FCSTD DOCUMENT  (FreeCAD 0.19R)
Label: plate_stand
License: All rights reserved
LicenseURL: http://en.wikipedia.org/wiki/All_rights_reserved
objects: App::Link×15, App::DocumentObjectGroup×2, PartDesign::CoordinateSystem×1, App::FeaturePython×1, App::Part×1
note: 1 computed .brp shape members not serialized (recipe doc carries the construction recipe); baked Part::Feature solids carry a one-line shape summary decoded from their .brp
EXTERNAL_REF file=column_60_60.FCStd obj=LCS_0
EXTERNAL_REF file=column_60_60.FCStd obj=____________Body
EXTERNAL_REF file=bridge_front.FCStd obj=LCS_middle
EXTERNAL_REF file=column_60_60.FCStd obj=LCS_bottom
EXTERNAL_REF file=bridge_front.FCStd obj=Body
EXTERNAL_REF file=bridge_front.FCStd obj=LCS_0
EXTERNAL_REF file=column_50_25.FCStd obj=LCS_bottom
EXTERNAL_REF file=column_50_25.FCStd obj=SmallColumnBody
EXTERNAL_REF file=column_60_60.FCStd obj=LCS_bottom_right
EXTERNAL_REF file=bridge_front.FCStd obj=LCS_0001
EXTERNAL_REF file=column_50_25.FCStd obj=LCS_bottom_narrow_2
EXTERNAL_REF file=bridge_front.FCStd obj=Body_bridge_side
EXTERNAL_REF file=column_50_25.FCStd obj=LCS_bottom_narrow1
EXTERNAL_REF file=bridge_front.FCStd obj=LCS_opp_side
EXTERNAL_REF file=bridge_front.FCStd obj=LCS_1
EXTERNAL_REF file=column_60_60.FCStd obj=LCS_1
EXTERNAL_REF file=bridge_front.FCStd obj=Body_2
EXTERNAL_REF file=column_60_60.FCStd obj=LCS_3
EXTERNAL_REF file=column_60_60.FCStd obj=LCS_2
EXTERNAL_REF file=column_60_60.FCStd obj=LCS_4

FEATURE [App::DocumentObjectGroup] Parts
FEATURE [PartDesign::CoordinateSystem] LCS_Origin
  AttacherType = Attacher::AttachEngine3D
  MapMode = 2
  Support = -> [X_Axis]
FEATURE [App::DocumentObjectGroup] Constraints
FEATURE [App::FeaturePython] Variables  # WARN: FeaturePython — macro-defined, semantics opaque (R4)
FEATURE [App::Link] column_60_60_ColumnBody
  AssemblyType = Asm4EE
  AttachedBy = #LCS_0
  AttachedTo = Parent Assembly#LCS_Origin
  LinkedObject = -> <external column_60_60.FCStd>#____________Body
  expr: Placement = LCS_Origin.Placement * AttachmentOffset * column_60_60#LCS_0.Placement ^ -1
FEATURE [App::Link] Unnamed_FrontBridgeBody
  AssemblyType = Asm4EE
  AttachedBy = #LCS_middle
  AttachedTo = column_60_60_ColumnBody#LCS_bottom
  AttachmentOffset = pos=(0,0,0) rot=(0,1,0;3.14159rad)
  LinkPlacement = pos=(-1.18e-14,-97.5,25) rot=(0,0,1;1.5708rad)
  LinkedObject = -> <external bridge_front.FCStd>#Body
  Placement = pos=(-1.18e-14,-97.5,25) rot=(0,0,1;1.5708rad)
  expr: Placement = column_60_60_ColumnBody.Placement * column_60_60#LCS_bottom.Placement * AttachmentOffset * bridge_front#LCS_middle.Placement ^ -1
FEATURE [App::Link] column_50_25_SmallColumnBody
  AssemblyType = Asm4EE
  AttachedBy = #LCS_bottom
  AttachedTo = Unnamed_FrontBridgeBody#LCS_0
  AttachmentOffset = pos=(0,0,0) rot=(-0.57735,-0.57735,-0.57735;4.18879rad)
  LinkPlacement = pos=(6.8e-15,-110,2.49e-14) rot=(0,0,-1;3.14159rad)
  LinkedObject = -> <external column_50_25.FCStd>#SmallColumnBody
  Placement = pos=(6.8e-15,-110,2.49e-14) rot=(0,0,-1;3.14159rad)
  expr: Placement = Unnamed_FrontBridgeBody.Placement * bridge_front#LCS_0.Placement * AttachmentOffset * column_50_25#LCS_bottom.Placement ^ -1
FEATURE [App::Link] bridge_front_FrontBridgeBody
  AssemblyType = Asm4EE
  AttachedBy = #LCS_middle
  AttachedTo = column_60_60_ColumnBody#LCS_bottom_right
  AttachmentOffset = pos=(0,0,0) rot=(1,0,0;3.14159rad)
  LinkPlacement = pos=(1.106e-12,97.5,25) rot=(-0.707107,0.707107,0;3.14159rad)
  LinkedObject = -> <external bridge_front.FCStd>#Body
  Placement = pos=(1.106e-12,97.5,25) rot=(-0.707107,0.707107,0;3.14159rad)
  expr: Placement = column_60_60_ColumnBody.Placement * column_60_60#LCS_bottom_right.Placement * AttachmentOffset * bridge_front#LCS_middle.Placement ^ -1
FEATURE [App::Link] column_50_25_SmallColumnBody001
  AssemblyType = Asm4EE
  AttachedBy = #LCS_bottom
  AttachedTo = bridge_front_FrontBridgeBody#LCS_0
  AttachmentOffset = pos=(0,0,0) rot=(0.57735,-0.57735,0.57735;4.18879rad)
  LinkPlacement = pos=(1.2532e-12,110,-2.84e-14) rot=(0,0,1;0rad)
  LinkedObject = -> <external column_50_25.FCStd>#SmallColumnBody
  Placement = pos=(1.2532e-12,110,-2.84e-14) rot=(0,0,1;0rad)
  expr: Placement = bridge_front_FrontBridgeBody.Placement * bridge_front#LCS_0.Placement * AttachmentOffset * column_50_25#LCS_bottom.Placement ^ -1
FEATURE [App::Link] bridge_front_Body_bridge_side
  AssemblyType = Asm4EE
  AttachedBy = #LCS_0001
  AttachedTo = column_50_25_SmallColumnBody#LCS_bottom_narrow_2
  AttachmentOffset = pos=(0,0,0) rot=(1,0,0;4.71239rad)
  LinkPlacement = pos=(25,-110,25) rot=(0,0,1;1.5708rad)
  LinkedObject = -> <external bridge_front.FCStd>#Body_bridge_side
  Placement = pos=(25,-110,25) rot=(0,0,1;1.5708rad)
  expr: Placement = column_50_25_SmallColumnBody.Placement * column_50_25#LCS_bottom_narrow_2.Placement * AttachmentOffset * bridge_front#LCS_0001.Placement ^ -1
FEATURE [App::Link] bridge_front_Body_bridge_side001
  AssemblyType = Asm4EE
  AttachedBy = #LCS_0001
  AttachedTo = column_50_25_SmallColumnBody001#LCS_bottom_narrow1
  AttachmentOffset = pos=(0,0,0) rot=(1,0,0;4.71239rad)
  LinkPlacement = pos=(25,110,25) rot=(0,0,-1;4.71239rad)
  LinkedObject = -> <external bridge_front.FCStd>#Body_bridge_side
  Placement = pos=(25,110,25) rot=(0,0,-1;4.71239rad)
  expr: Placement = column_50_25_SmallColumnBody001.Placement * column_50_25#LCS_bottom_narrow1.Placement * AttachmentOffset * bridge_front#LCS_0001.Placement ^ -1
FEATURE [App::Link] column_60_60_ColumnBody001
  AssemblyType = Asm4EE
  AttachedBy = #LCS_bottom_right
  AttachedTo = bridge_front_Body_bridge_side#LCS_opp_side
  AttachmentOffset = pos=(0,0,0) rot=(0,1,0;3.14159rad)
  LinkPlacement = pos=(220,-110,2.771e-13) rot=(0,0,1;1.5708rad)
  LinkedObject = -> <external column_60_60.FCStd>#____________Body
  Placement = pos=(220,-110,2.771e-13) rot=(0,0,1;1.5708rad)
  expr: Placement = bridge_front_Body_bridge_side.Placement * bridge_front#LCS_opp_side.Placement * AttachmentOffset * column_60_60#LCS_bottom_right.Placement ^ -1
FEATURE [App::Link] column_60_60_ColumnBody002
  AssemblyType = Asm4EE
  AttachedBy = #LCS_bottom
  AttachedTo = bridge_front_Body_bridge_side001#LCS_opp_side
  AttachmentOffset = pos=(0,0,0) rot=(0,1,0;3.14159rad)
  LinkPlacement = pos=(220,110,1.315e-13) rot=(0,0,-1;1.5708rad)
  LinkedObject = -> <external column_60_60.FCStd>#____________Body
  Placement = pos=(220,110,1.315e-13) rot=(0,0,-1;1.5708rad)
  expr: Placement = bridge_front_Body_bridge_side001.Placement * bridge_front#LCS_opp_side.Placement * AttachmentOffset * column_60_60#LCS_bottom.Placement ^ -1
FEATURE [App::Link] bridge_front_Body_bridge_back
  AssemblyType = Asm4EE
  AttachedBy = #LCS_1
  AttachedTo = column_60_60_ColumnBody002#LCS_1
  AttachmentOffset = pos=(0,0,0) rot=(0,1,0;3.14159rad)
  LinkPlacement = pos=(220,-80,25) rot=(0,0,1;3.14159rad)
  LinkedObject = -> <external bridge_front.FCStd>#Body_2
  Placement = pos=(220,-80,25) rot=(0,0,1;3.14159rad)
  expr: Placement = column_60_60_ColumnBody002.Placement * column_60_60#LCS_1.Placement * AttachmentOffset * bridge_front#LCS_1.Placement ^ -1
FEATURE [App::Link] bridge_front_Body_bridge_back001
  AssemblyType = Asm4EE
  AttachedBy = #LCS_1
  AttachedTo = column_60_60_ColumnBody001#LCS_3
  AttachmentOffset = pos=(0,0,0) rot=(0.707107,0,0.707107;3.14159rad)
  LinkPlacement = pos=(223,80,675) rot=(0,1,0;3.14159rad)
  LinkedObject = -> <external bridge_front.FCStd>#Body_2
  Placement = pos=(223,80,675) rot=(0,1,0;3.14159rad)
  expr: Placement = column_60_60_ColumnBody001.Placement * column_60_60#LCS_3.Placement * AttachmentOffset * bridge_front#LCS_1.Placement ^ -1
FEATURE [App::Link] bridge_front_Body_bridge_side002
  AssemblyType = Asm4EE
  AttachedBy = #LCS_0001
  AttachedTo = column_60_60_ColumnBody001#LCS_2
  AttachmentOffset = pos=(0,0,0) rot=(-0.57735,-0.57735,0.57735;4.18879rad)
  LinkPlacement = pos=(190,-107,675) rot=(0.707107,0.707107,0;3.14159rad)
  LinkedObject = -> <external bridge_front.FCStd>#Body_bridge_side
  Placement = pos=(190,-107,675) rot=(0.707107,0.707107,0;3.14159rad)
  expr: Placement = column_60_60_ColumnBody001.Placement * column_60_60#LCS_2.Placement * AttachmentOffset * bridge_front#LCS_0001.Placement ^ -1
FEATURE [App::Link] bridge_front_Body_bridge_side003
  AssemblyType = Asm4EE
  AttachedBy = #LCS_0001
  AttachedTo = column_60_60_ColumnBody002#LCS_4
  AttachmentOffset = pos=(0,0,0) rot=(0.57735,0.57735,0.57735;4.18879rad)
  LinkPlacement = pos=(190,113,675) rot=(0,0,1;4.71239rad)
  LinkedObject = -> <external bridge_front.FCStd>#Body_bridge_side
  Placement = pos=(190,113,675) rot=(0,0,1;4.71239rad)
  expr: Placement = column_60_60_ColumnBody002.Placement * column_60_60#LCS_4.Placement * AttachmentOffset * bridge_front#LCS_0001.Placement ^ -1
FEATURE [App::Link] bridge_front_FrontBridgeBody001
  AssemblyType = Asm4EE
  AttachedBy = #LCS_middle
  AttachedTo = column_60_60_ColumnBody#LCS_2
  AttachmentOffset = pos=(0,0,0) rot=(0,1,0;1.5708rad)
  LinkPlacement = pos=(3,97.5,675) rot=(0,0,1;4.71239rad)
  LinkedObject = -> <external bridge_front.FCStd>#Body
  Placement = pos=(3,97.5,675) rot=(0,0,1;4.71239rad)
  expr: Placement = column_60_60_ColumnBody.Placement * column_60_60#LCS_2.Placement * AttachmentOffset * bridge_front#LCS_middle.Placement ^ -1
FEATURE [App::Link] bridge_front_FrontBridgeBody002
  AssemblyType = Asm4EE
  AttachedBy = #LCS_middle
  AttachedTo = column_60_60_ColumnBody#LCS_4
  AttachmentOffset = pos=(0,0,0) rot=(0,1,0;1.5708rad)
  LinkPlacement = pos=(-3,-97.5,675) rot=(0,0,1;1.5708rad)
  LinkedObject = -> <external bridge_front.FCStd>#Body
  Placement = pos=(-3,-97.5,675) rot=(0,0,1;1.5708rad)
  expr: Placement = column_60_60_ColumnBody.Placement * column_60_60#LCS_4.Placement * AttachmentOffset * bridge_front#LCS_middle.Placement ^ -1
FEATURE [App::Part] Model
  Configuration = 0
  Group = -> [LCS_Origin,Constraints,Variables,column_60_60_ColumnBody,Unnamed_FrontBridgeBody,column_50_25_SmallColumnBody,bridge_front_FrontBridgeBody,column_50_25_SmallColumnBody001,bridge_front_Body_bridge_side,bridge_front_Body_bridge_side001,column_60_60_ColumnBody001,column_60_60_ColumnBody002,bridge_front_Body_bridge_back,bridge_front_Body_bridge_back001,bridge_front_Body_bridge_side002,+3 more]
  Origin = -> Origin
  Type = Assembly4 Model

RESOLVED EXTERNAL PARTS (link-assembly join: the EXTERNAL_REF files above that resolve inside this repo's crawl, each included once):
---- part bridge_front.FCStd = doc fcstd_2d3e780000c6 ----
FCSTD DOCUMENT  (FreeCAD 0.19R)
Label: bridge_front
License: All rights reserved
LicenseURL: http://en.wikipedia.org/wiki/All_rights_reserved
objects: PartDesign::CoordinateSystem×6, Sketcher::SketchObject×3, PartDesign::Pad×3, PartDesign::Body×3
note: 18 computed .brp shape members not serialized (recipe doc carries the construction recipe); baked Part::Feature solids carry a one-line shape summary decoded from their .brp

FEATURE [PartDesign::CoordinateSystem] LCS_0
  AttacherType = Attacher::AttachEngine3D
  MapMode = 2
  Support = -> [X_Axis]
FEATURE [Sketcher::SketchObject] Sketch
  FullyConstrained = true
  MapMode = 5
  Placement = pos=(0,0,0) rot=(0.57735,0.57735,0.57735;2.0944rad)
  Support = -> [YZ_Plane]
  sketch-geometry (8):
    g0: LineSegment StartX=-8 StartY=20 StartZ=0 EndX=8 EndY=20 EndZ=0
    g1: LineSegment StartX=10 StartY=18 StartZ=0 EndX=10 EndY=-18 EndZ=0
    g2: LineSegment StartX=8 StartY=-20 StartZ=0 EndX=-8 EndY=-20 EndZ=0
    g3: LineSegment StartX=-10 StartY=-18 StartZ=0 EndX=-10 EndY=18 EndZ=0
    g4: ArcOfCircle CenterX=-8 CenterY=18 CenterZ=0 NormalX=0 NormalY=0 NormalZ=1 AngleXU=0 Radius=2 StartAngle=1.5708 EndAngle=3.14159
    g5: ArcOfCircle CenterX=-8 CenterY=-18 CenterZ=0 NormalX=0 NormalY=0 NormalZ=1 AngleXU=0 Radius=2 StartAngle=3.14159 EndAngle=4.71239
    g6: ArcOfCircle CenterX=8 CenterY=-18 CenterZ=0 NormalX=0 NormalY=0 NormalZ=1 AngleXU=0 Radius=2 StartAngle=4.71239 EndAngle=6.28319
    g7: ArcOfCircle CenterX=8 CenterY=18 CenterZ=0 NormalX=0 NormalY=0 NormalZ=1 AngleXU=0 Radius=2 StartAngle=-4.71e-14 EndAngle=1.5708
  constraints (18):
    c: Horizontal(g0)
    c: Horizontal(g2)
    c: Vertical(g1)
    c: Vertical(g3)
    c: Tangent(g0,g4) = 1.5708
    c: Tangent(g3,g4) = 1.5708
    c: Tangent(g3,g5) = 1.5708
    c: Tangent(g2,g5) = 1.5708
    c: Tangent(g1,g6) = 1.5708
    c: Tangent(g2,g6) = 1.5708
    c: Tangent(g0,g7) = 1.5708
    c: Tangent(g1,g7) = 1.5708
    c: Radius(g6) = 2
    c: Equal(g6,g5)
    c: DistanceY(g2,g0) = 40
    c: DistanceX(g3,g1) = 20
    c: Symmetric(g3,g1,g-2)
    c: Symmetric(g2,g0,g-1)
FEATURE [PartDesign::Pad] Pad
  Direction = (1,1,1)
  Length = 67.5
  Length2 = 100
  Placement = pos=(0,0,0) rot=(0.57735,0.57735,0.57735;2.0944rad)
  Profile = -> Sketch
  Type = 0
FEATURE [PartDesign::CoordinateSystem] LCS_middle
  AttacherType = Attacher::AttachEngine3D
  MapMode = 5
  Placement = pos=(67.5,-3e-14,2.25e-14) rot=(0.57735,0.57735,0.57735;2.0944rad)
  Support = -> [Pad]
FEATURE [PartDesign::Body] Body  label="FrontBridgeBody"
  Group = -> [LCS_0,Sketch,Pad,LCS_middle]
  Origin = -> Origin
  Tip = -> Pad
FEATURE [PartDesign::CoordinateSystem] LCS_0001
  AttacherType = Attacher::AttachEngine3D
  MapMode = 2
  Support = -> [X_Axis001]
FEATURE [Sketcher::SketchObject] Sketch001
  FullyConstrained = true
  MapMode = 5
  Placement = pos=(0,0,0) rot=(1,0,0;1.5708rad)
  Support = -> [XZ_Plane001]
  sketch-geometry (8):
    g0: LineSegment StartX=-8 StartY=20 StartZ=0 EndX=8 EndY=20 EndZ=0
    g1: LineSegment StartX=10 StartY=18 StartZ=0 EndX=10 EndY=-18 EndZ=0
    g2: LineSegment StartX=8 StartY=-20 StartZ=0 EndX=-8 EndY=-20 EndZ=0
    g3: LineSegment StartX=-10 StartY=-18 StartZ=0 EndX=-10 EndY=18 EndZ=0
    g4: ArcOfCircle CenterX=-8 CenterY=-18 CenterZ=0 NormalX=0 NormalY=0 NormalZ=1 AngleXU=0 Radius=2 StartAngle=3.14159 EndAngle=4.71239
    g5: ArcOfCircle CenterX=8 CenterY=-18 CenterZ=0 NormalX=0 NormalY=0 NormalZ=1 AngleXU=0 Radius=2 StartAngle=4.71239 EndAngle=6.28319
    g6: ArcOfCircle CenterX=8 CenterY=18 CenterZ=0 NormalX=0 NormalY=0 NormalZ=1 AngleXU=0 Radius=2 StartAngle=0 EndAngle=1.5708
    g7: ArcOfCircle CenterX=-8 CenterY=18 CenterZ=0 NormalX=0 NormalY=0 NormalZ=1 AngleXU=0 Radius=2 StartAngle=1.5708 EndAngle=3.14159
  constraints (18):
    c: Horizontal(g0)
    c: Horizontal(g2)
    c: Vertical(g1)
    c: Vertical(g3)
    c: Tangent(g3,g4) = 1.5708
    c: Tangent(g2,g4) = 1.5708
    c: Tangent(g2,g5) = 1.5708
    c: Tangent(g1,g5) = 1.5708
    c: Tangent(g0,g6) = 1.5708
    c: Tangent(g1,g6) = 1.5708
    c: Tangent(g3,g7) = 1.5708
    c: Tangent(g0,g7) = 1.5708
    c: Radius(g6) = 2
    c: Equal(g6,g7)
    c: DistanceY(g2,g0) = 40
    c: DistanceX(g3,g1) = 20
    c: Symmetric(g0,g2,g-1)
    c: Symmetric(g3,g1,g-2)
FEATURE [PartDesign::Pad] Pad001
  Direction = (1,1,1)
  Length = 165
  Length2 = 100
  Placement = pos=(0,0,0) rot=(1,0,0;1.5708rad)
  Profile = -> Sketch001
  Type = 0
FEATURE [PartDesign::CoordinateSystem] LCS_opp_side
  AttacherType = Attacher::AttachEngine3D
  MapMode = 5
  Placement = pos=(0,-165,1.099e-13) rot=(1,0,0;1.5708rad)
  Support = -> [Pad001]
FEATURE [PartDesign::Body] Body_bridge_side
  Group = -> [LCS_0001,Sketch001,Pad001,LCS_opp_side]
  Origin = -> Origin001
  Tip = -> Pad001
FEATURE [PartDesign::CoordinateSystem] LCS_0002
  AttacherType = Attacher::AttachEngine3D
  MapMode = 2
  Support = -> [X_Axis002]
FEATURE [Sketcher::SketchObject] Sketch002
  FullyConstrained = true
  MapMode = 5
  Placement = pos=(0,0,0) rot=(1,0,0;1.5708rad)
  Support = -> [XZ_Plane002]
  sketch-geometry (8):
    g0: LineSegment StartX=-8 StartY=20 StartZ=0 EndX=8 EndY=20 EndZ=0
    g1: LineSegment StartX=10 StartY=18 StartZ=0 EndX=10 EndY=-18 EndZ=0
    g2: LineSegment StartX=8 StartY=-20 StartZ=0 EndX=-8 EndY=-20 EndZ=0
    g3: LineSegment StartX=-10 StartY=-18 StartZ=0 EndX=-10 EndY=18 EndZ=0
    g4: ArcOfCircle CenterX=-8 CenterY=18 CenterZ=0 NormalX=0 NormalY=0 NormalZ=1 AngleXU=0 Radius=2 StartAngle=1.5708 EndAngle=3.14159
    g5: ArcOfCircle CenterX=-8 CenterY=-18 CenterZ=0 NormalX=0 NormalY=0 NormalZ=1 AngleXU=0 Radius=2 StartAngle=3.14159 EndAngle=4.71239
    g6: ArcOfCircle CenterX=8 CenterY=-18 CenterZ=0 NormalX=0 NormalY=0 NormalZ=1 AngleXU=0 Radius=2 StartAngle=4.71239 EndAngle=6.28319
    g7: ArcOfCircle CenterX=8 CenterY=18 CenterZ=0 NormalX=0 NormalY=0 NormalZ=1 AngleXU=0 Radius=2 StartAngle=0 EndAngle=1.5708
  constraints (18):
    c: Horizontal(g0)
    c: Horizontal(g2)
    c: Vertical(g1)
    c: Vertical(g3)
    c: Tangent(g0,g4) = 1.5708
    c: Tangent(g3,g4) = 1.5708
    c: Tangent(g3,g5) = 1.5708
    c: Tangent(g2,g5) = 1.5708
    c: Tangent(g2,g6) = 1.5708
    c: Tangent(g1,g6) = 1.5708
    c: Tangent(g1,g7) = 1.5708
    c: Tangent(g0,g7) = 1.5708
    c: Radius(g4) = 2
    c: Equal(g4,g7)
    c: DistanceX(g3,g1) = 20
    c: DistanceY(g2,g0) = 40
    c: Symmetric(g2,g0,g-1)
    c: Symmetric(g3,g1,g-2)
FEATURE [PartDesign::Pad] Pad002
  Direction = (1,1,1)
  Length = 160
  Length2 = 100
  Placement = pos=(0,0,0) rot=(1,0,0;1.5708rad)
  Profile = -> Sketch002
  Type = 0
FEATURE [PartDesign::CoordinateSystem] LCS_1
  AttacherType = Attacher::AttachEngine3D
  MapMode = 5
  Placement = pos=(0,-160,1.066e-13) rot=(1,0,0;1.5708rad)
  Support = -> [Pad002]
FEATURE [PartDesign::Body] Body_2  label="Body_bridge_back"
  Group = -> [LCS_0002,Sketch002,Pad002,LCS_1]
  Origin = -> Origin002
  Tip = -> Pad002
---- part column_50_25.FCStd = doc fcstd_75b4c7ce69b3 ----
FCSTD DOCUMENT  (FreeCAD 0.19R)
Label: column_50_25
License: All rights reserved
LicenseURL: http://en.wikipedia.org/wiki/All_rights_reserved
objects: PartDesign::CoordinateSystem×4, Sketcher::SketchObject×1, PartDesign::Pad×1, PartDesign::Body×1
note: 8 computed .brp shape members not serialized (recipe doc carries the construction recipe); baked Part::Feature solids carry a one-line shape summary decoded from their .brp

FEATURE [PartDesign::CoordinateSystem] LCS_0
  AttacherType = Attacher::AttachEngine3D
  MapMode = 2
  Support = -> [X_Axis]
FEATURE [Sketcher::SketchObject] Sketch
  FullyConstrained = true
  MapMode = 5
  Support = -> [XY_Plane]
  sketch-geometry (8):
    g0: LineSegment StartX=-23 StartY=12.5 StartZ=0 EndX=23 EndY=12.5 EndZ=0
    g1: LineSegment StartX=25 StartY=10.5 StartZ=0 EndX=25 EndY=-10.5 EndZ=0
    g2: LineSegment StartX=23 StartY=-12.5 StartZ=0 EndX=-23 EndY=-12.5 EndZ=0
    g3: LineSegment StartX=-25 StartY=-10.5 StartZ=0 EndX=-25 EndY=10.5 EndZ=0
    g4: ArcOfCircle CenterX=-23 CenterY=10.5 CenterZ=0 NormalX=0 NormalY=0 NormalZ=1 AngleXU=0 Radius=2 StartAngle=1.5708 EndAngle=3.14159
    g5: ArcOfCircle CenterX=-23 CenterY=-10.5 CenterZ=0 NormalX=0 NormalY=0 NormalZ=1 AngleXU=0 Radius=2 StartAngle=3.14159 EndAngle=4.71239
    g6: ArcOfCircle CenterX=23 CenterY=-10.5 CenterZ=0 NormalX=0 NormalY=0 NormalZ=1 AngleXU=0 Radius=2 StartAngle=4.71239 EndAngle=6.28319
    g7: ArcOfCircle CenterX=23 CenterY=10.5 CenterZ=0 NormalX=0 NormalY=0 NormalZ=1 AngleXU=0 Radius=2 StartAngle=0 EndAngle=1.5708
  constraints (18):
    c: Horizontal(g0)
    c: Horizontal(g2)
    c: Vertical(g1)
    c: Vertical(g3)
    c: Tangent(g3,g4) = 1.5708
    c: Tangent(g0,g4) = 1.5708
    c: Tangent(g2,g5) = 1.5708
    c: Tangent(g3,g5) = 1.5708
    c: Tangent(g1,g6) = 1.5708
    c: Tangent(g2,g6) = 1.5708
    c: Tangent(g0,g7) = 1.5708
    c: Tangent(g1,g7) = 1.5708
    c: Radius(g4) = 2
    c: Equal(g4,g7)
    c: DistanceY(g2,g0) = 25
    c: DistanceX(g3,g1) = 50
    c: Symmetric(g2,g0,g-1)
    c: Symmetric(g3,g1,g-2)
FEATURE [PartDesign::Pad] Pad
  Direction = (1,1,1)
  Length = 700
  Length2 = 100
  Profile = -> Sketch
  Type = 0
FEATURE [PartDesign::CoordinateSystem] LCS_bottom
  AttacherType = Attacher::AttachEngine3D
  AttachmentOffset = pos=(0,25,0) rot=(0,0,1;0rad)
  MapMode = 5
  Placement = pos=(0,-12.5,25) rot=(1,0,0;1.5708rad)
  Support = -> [Pad]
FEATURE [PartDesign::CoordinateSystem] LCS_bottom_narrow1
  AttacherType = Attacher::AttachEngine3D
  AttachmentOffset = pos=(0,25,0) rot=(0,0,1;0rad)
  MapMode = 5
  Placement = pos=(25,0,25) rot=(0.57735,0.57735,0.57735;2.0944rad)
  Support = -> [Pad]
FEATURE [PartDesign::CoordinateSystem] LCS_bottom_narrow_2
  AttacherType = Attacher::AttachEngine3D
  AttachmentOffset = pos=(0,25,0) rot=(0,0,1;0rad)
  MapMode = 5
  Placement = pos=(-25,0,25) rot=(0.57735,-0.57735,-0.57735;2.0944rad)
  Support = -> [Pad]
FEATURE [PartDesign::Body] SmallColumnBody
  Group = -> [LCS_0,Sketch,Pad,LCS_bottom,LCS_bottom_narrow1,LCS_bottom_narrow_2]
  Origin = -> Origin
  Tip = -> Pad
---- part column_60_60.FCStd = doc fcstd_8bc984a64163 ----
FCSTD DOCUMENT  (FreeCAD 0.19R)
Label: column_60_60
License: All rights reserved
LicenseURL: http://en.wikipedia.org/wiki/All_rights_reserved
objects: PartDesign::CoordinateSystem×7, Sketcher::SketchObject×1, PartDesign::Pad×1, PartDesign::Body×1
note: 11 computed .brp shape members not serialized (recipe doc carries the construction recipe); baked Part::Feature solids carry a one-line shape summary decoded from their .brp

FEATURE [PartDesign::CoordinateSystem] LCS_0
  AttacherType = Attacher::AttachEngine3D
  MapMode = 2
  Support = -> [X_Axis]
FEATURE [Sketcher::SketchObject] Sketch
  FullyConstrained = true
  MapMode = 5
  Support = -> [XY_Plane]
  sketch-geometry (8):
    g0: LineSegment StartX=-27 StartY=30 StartZ=0 EndX=27 EndY=30 EndZ=0
    g1: LineSegment StartX=30 StartY=27 StartZ=0 EndX=30 EndY=-27 EndZ=0
    g2: LineSegment StartX=27 StartY=-30 StartZ=0 EndX=-27 EndY=-30 EndZ=0
    g3: LineSegment StartX=-30 StartY=-27 StartZ=0 EndX=-30 EndY=27 EndZ=0
    g4: ArcOfCircle CenterX=-27 CenterY=27 CenterZ=0 NormalX=0 NormalY=0 NormalZ=1 AngleXU=0 Radius=3 StartAngle=1.5708 EndAngle=3.14159
    g5: ArcOfCircle CenterX=-27 CenterY=-27 CenterZ=0 NormalX=0 NormalY=0 NormalZ=1 AngleXU=0 Radius=3 StartAngle=3.14159 EndAngle=4.71239
    g6: ArcOfCircle CenterX=27 CenterY=-27 CenterZ=0 NormalX=0 NormalY=0 NormalZ=1 AngleXU=0 Radius=3 StartAngle=4.71239 EndAngle=6.28319
    g7: ArcOfCircle CenterX=27 CenterY=27 CenterZ=0 NormalX=0 NormalY=0 NormalZ=1 AngleXU=0 Radius=3 StartAngle=-1.394e-13 EndAngle=1.5708
  constraints (18):
    c: Horizontal(g2)
    c: Vertical(g3)
    c: Tangent(g3,g4) = 1.5708
    c: Tangent(g0,g4) = 1.5708
    c: Tangent(g3,g5) = 1.5708
    c: Tangent(g2,g5) = 1.5708
    c: Tangent(g2,g6) = 1.5708
    c: Tangent(g1,g6) = 1.5708
    c: Tangent(g1,g7) = 1.5708
    c: Tangent(g0,g7) = 1.5708
    c: Radius(g4) = 3
    c: Equal(g4,g7)
    c: Equal(g4,g6)
    c: Equal(g4,g5)
    c: DistanceY(g2,g0) = 60
    c: DistanceX(g3,g1) = 60
    c: Symmetric(g2,g0,g-1)
    c: Symmetric(g3,g1,g-2)
FEATURE [PartDesign::Pad] Pad
  Direction = (1,1,1)
  Length = 700
  Length2 = 100
  Profile = -> Sketch
  Type = 0
FEATURE [PartDesign::CoordinateSystem] LCS_bottom  label="LCS_bottom_left"
  AttacherType = Attacher::AttachEngine3D
  AttachmentOffset = pos=(0,25,0) rot=(0,0,1;0rad)
  MapMode = 5
  Placement = pos=(0,-30,25) rot=(1,0,0;1.5708rad)
  Support = -> [Pad]
FEATURE [PartDesign::CoordinateSystem] LCS_bottom_right
  AttacherType = Attacher::AttachEngine3D
  AttachmentOffset = pos=(0,25,0) rot=(0,0,1;0rad)
  MapMode = 5
  Placement = pos=(3.414e-13,30,25) rot=(0,0.707107,0.707107;3.14159rad)
  Support = -> [Pad]
FEATURE [PartDesign::CoordinateSystem] LCS_1
  AttacherType = Attacher::AttachEngine3D
  AttachmentOffset = pos=(0,25,0) rot=(0,0,1;0rad)
  MapMode = 5
  Placement = pos=(30,-4.789e-12,25) rot=(0.57735,0.57735,0.57735;2.0944rad)
  Support = -> [Pad]
FEATURE [PartDesign::CoordinateSystem] LCS_2
  AttacherType = Attacher::AttachEngine3D
  AttachmentOffset = pos=(0,-25,-30) rot=(0,0,1;0rad)
  MapMode = 7
  Placement = pos=(3,30,675) rot=(-0.57735,0.57735,0.57735;4.18879rad)
  Support = -> [Pad]
FEATURE [PartDesign::CoordinateSystem] LCS_3
  AttacherType = Attacher::AttachEngine3D
  AttachmentOffset = pos=(0,-25,-30) rot=(0,0,1;0rad)
  MapMode = 7
  Placement = pos=(30,-3,675) rot=(0,0.707107,0.707107;3.14159rad)
  Support = -> [Pad]
FEATURE [PartDesign::CoordinateSystem] LCS_4
  AttacherType = Attacher::AttachEngine3D
  AttachmentOffset = pos=(0,-25,-30) rot=(0,0,1;0rad)
  MapMode = 7
  Placement = pos=(-3,-30,675) rot=(0.57735,0.57735,0.57735;2.0944rad)
  Support = -> [Pad]
FEATURE [PartDesign::Body] ____________Body  label="ColumnBody"
  Group = -> [LCS_0,Sketch,Pad,LCS_bottom,LCS_bottom_right,LCS_1,LCS_2,LCS_3,LCS_4]
  Origin = -> Origin
  Tip = -> Pad
